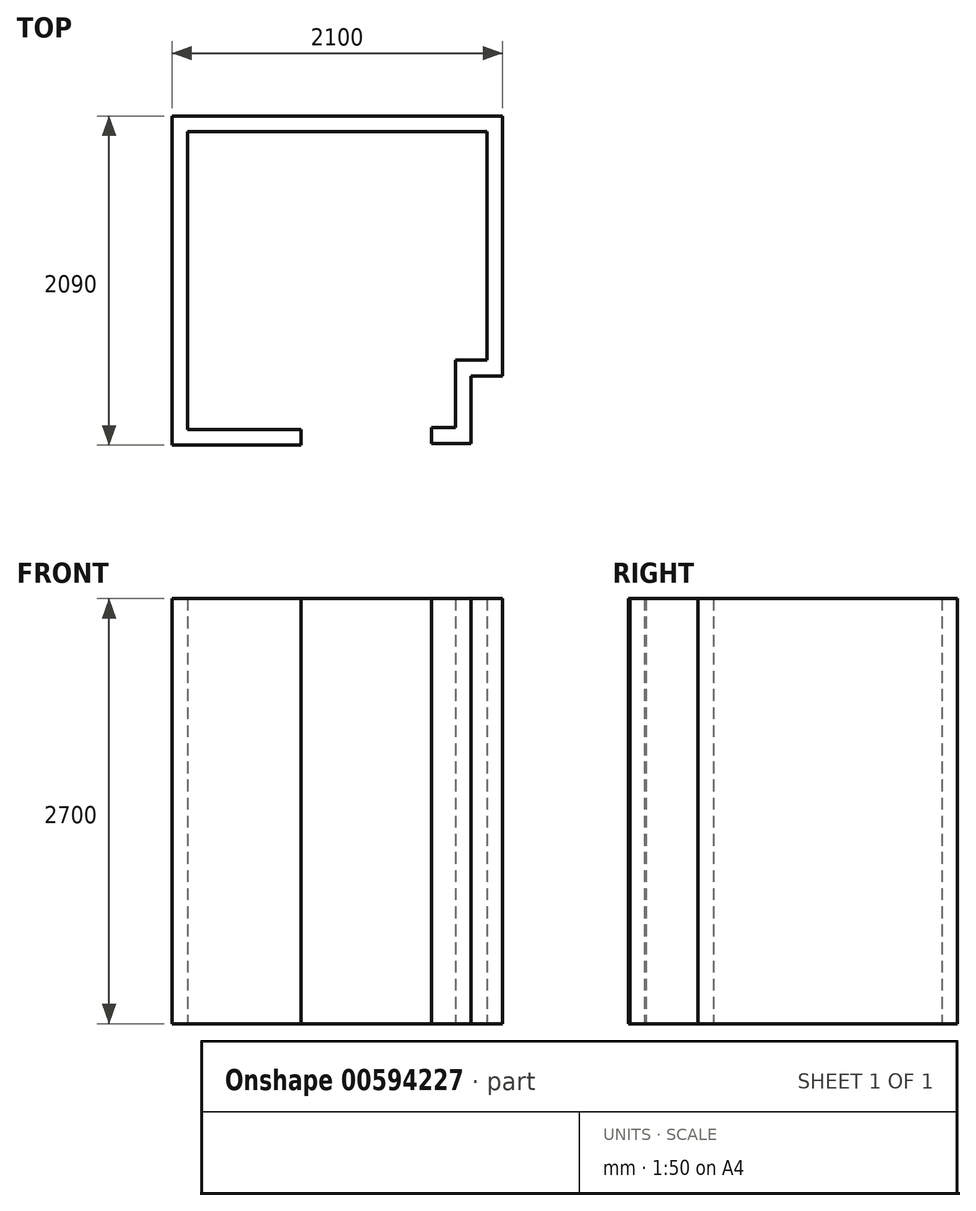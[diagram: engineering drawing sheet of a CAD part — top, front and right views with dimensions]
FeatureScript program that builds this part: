
annotation { "Feature Type Name" : "Feature", "Feature Type Description" : "" }
export const myFeature = defineFeature(function(context is Context, id is Id, definition is map)
    precondition{}
    {
        {
            var Q0;
            Q0=qCreatedBy(makeId("Top.planeOp"),FACE);
            var sketch = newSketch(context, id + "F0", { "sketchPlane" : qUnion([Q0])});
            skLineSegment(sketch, "E0", {"start": v(0, 0) * mm, "end": v(-720, 0) * mm});
            skLineSegment(sketch, "E1", {"start": v(-720, 0) * mm, "end": v(-720, 1890) * mm});
            skLineSegment(sketch, "E2", {"start": v(-720, 1890) * mm, "end": v(1180, 1890) * mm});
            skLineSegment(sketch, "E3", {"start": v(1180, 1890) * mm, "end": v(1180, 440) * mm});
            skLineSegment(sketch, "E4", {"start": v(1180, 440) * mm, "end": v(980, 440) * mm});
            skLineSegment(sketch, "E5", {"start": v(980, 440) * mm, "end": v(980, 10) * mm});
            skLineSegment(sketch, "E6", {"start": v(980, 10) * mm, "end": v(830, 10) * mm});
            skLineSegment(sketch, "E7", {"start": v(830, 10) * mm, "end": v(830, -90) * mm});
            skLineSegment(sketch, "E8.0", {"start": v(1080, -90) * mm, "end": v(830, -90) * mm});
            skLineSegment(sketch, "E8.1", {"start": v(1080, 340) * mm, "end": v(1080, -90) * mm});
            skLineSegment(sketch, "E8.2", {"start": v(1280, 340) * mm, "end": v(1080, 340) * mm});
            skLineSegment(sketch, "E8.3", {"start": v(0, -100) * mm, "end": v(-820, -100) * mm});
            skLineSegment(sketch, "E8.4", {"start": v(-820, -100) * mm, "end": v(-820, 1990) * mm});
            skLineSegment(sketch, "E8.5", {"start": v(-820, 1990) * mm, "end": v(1280, 1990) * mm});
            skLineSegment(sketch, "E8.6", {"start": v(1280, 1990) * mm, "end": v(1280, 340) * mm});
            skLineSegment(sketch, "E9", {"start": v(0, 0) * mm, "end": v(0, -100) * mm});
            skSolve(sketch);
        }
        {
            var Q0;
            Q0 = qSketchRegion(id + "F0", true);
            extrude(context, id + "F1", {"entities" : qUnion([Q0]), "depth" : 2700 * mm, "offsetDistance" : 25 * mm});
        }
        {
            var Q0;
            Q0=qCreatedBy(makeId("Top.planeOp"),FACE);
            var sketch = newSketch(context, id + "F2", { "sketchPlane" : qUnion([Q0])});
            skLineSegment(sketch, "E10.bottom", {"start": v(-720, 1000) * mm, "end": v(-166, 1000) * mm});
            skLineSegment(sketch, "E10.top", {"start": v(-720, 100) * mm, "end": v(-166, 100) * mm});
            skLineSegment(sketch, "E10.left", {"start": v(-720, 1000) * mm, "end": v(-720, 100) * mm});
            skLineSegment(sketch, "E10.right", {"start": v(-166, 1000) * mm, "end": v(-166, 100) * mm});
            skLineSegment(sketch, "E11.bottom", {"start": v(730, 1000) * mm, "end": v(1180, 1000) * mm});
            skLineSegment(sketch, "E11.top", {"start": v(730, 550) * mm, "end": v(1180, 550) * mm});
            skLineSegment(sketch, "E11.left", {"start": v(730, 1000) * mm, "end": v(730, 550) * mm});
            skLineSegment(sketch, "E11.right", {"start": v(1180, 1000) * mm, "end": v(1180, 550) * mm});
            skLineSegment(sketch, "E12.bottom", {"start": v(-165, 1000) * mm, "end": v(-147, 1000) * mm});
            skLineSegment(sketch, "E12.top", {"start": v(-165, 551.5) * mm, "end": v(-147, 551.5) * mm});
            skLineSegment(sketch, "E12.left", {"start": v(-165, 1000) * mm, "end": v(-165, 551.5) * mm});
            skLineSegment(sketch, "E12.right", {"start": v(-147, 1000) * mm, "end": v(-147, 551.5) * mm});
            skLineSegment(sketch, "E13.bottom", {"start": v(-165, 548.5) * mm, "end": v(-147, 548.5) * mm});
            skLineSegment(sketch, "E13.top", {"start": v(-165, 100) * mm, "end": v(-147, 100) * mm});
            skLineSegment(sketch, "E13.left", {"start": v(-165, 548.5) * mm, "end": v(-165, 100) * mm});
            skLineSegment(sketch, "E13.right", {"start": v(-147, 548.5) * mm, "end": v(-147, 100) * mm});
            skLineSegment(sketch, "E14.bottom", {"start": v(711, 1000) * mm, "end": v(729, 1000) * mm});
            skLineSegment(sketch, "E14.top", {"start": v(711, 551.5) * mm, "end": v(729, 551.5) * mm});
            skLineSegment(sketch, "E14.left", {"start": v(711, 1000) * mm, "end": v(711, 551.5) * mm});
            skLineSegment(sketch, "E14.right", {"start": v(729, 1000) * mm, "end": v(729, 551.5) * mm});
            skSolve(sketch);
        }
    });
